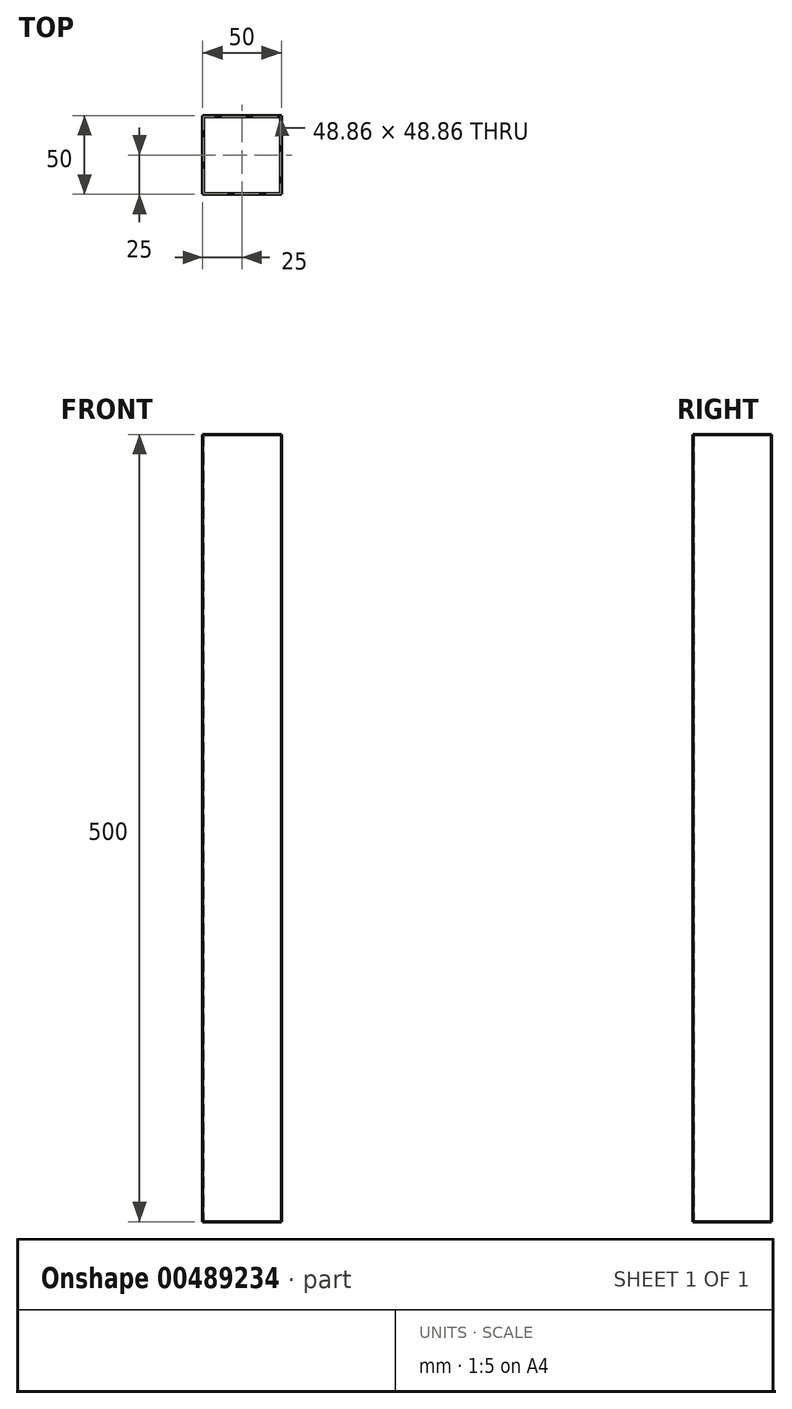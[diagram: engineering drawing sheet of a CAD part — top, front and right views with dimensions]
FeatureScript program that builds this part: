
annotation { "Feature Type Name" : "Feature", "Feature Type Description" : "" }
export const myFeature = defineFeature(function(context is Context, id is Id, definition is map)
    precondition{}
    {
        {
            var Q0;
            Q0=qCreatedBy(makeId("Top.planeOp"),FACE);
            var sketch = newSketch(context, id + "F0", { "sketchPlane" : qUnion([Q0])});
            skLineSegment(sketch, "E0.bottom", {"start": v(0, 0) * mm, "end": v(50, 0) * mm});
            skLineSegment(sketch, "E0.top", {"start": v(0, -50) * mm, "end": v(50, -50) * mm});
            skLineSegment(sketch, "E0.left", {"start": v(0, 0) * mm, "end": v(0, -50) * mm});
            skLineSegment(sketch, "E0.right", {"start": v(50, 0) * mm, "end": v(50, -50) * mm});
            skLineSegment(sketch, "E1.0", {"start": v(0.57, -49.43) * mm, "end": v(49.43, -49.43) * mm});
            skLineSegment(sketch, "E1.1", {"start": v(0.57, -0.57) * mm, "end": v(0.57, -49.43) * mm});
            skLineSegment(sketch, "E1.2", {"start": v(0.57, -0.57) * mm, "end": v(49.43, -0.57) * mm});
            skLineSegment(sketch, "E1.3", {"start": v(49.43, -0.57) * mm, "end": v(49.43, -49.43) * mm});
            skLineSegment(sketch, "E2.0", {"start": v(2.57, -47.43) * mm, "end": v(47.43, -47.43) * mm});
            skLineSegment(sketch, "E2.1", {"start": v(2.57, -2.57) * mm, "end": v(2.57, -47.43) * mm});
            skLineSegment(sketch, "E2.2", {"start": v(2.57, -2.57) * mm, "end": v(47.43, -2.57) * mm});
            skLineSegment(sketch, "E2.3", {"start": v(47.43, -2.57) * mm, "end": v(47.43, -47.43) * mm});
            skSolve(sketch);
        }
        {
            var Q0;
            Q0 = qSketchRegion(id + "F0", true);
            extrude(context, id + "F1", {"entities" : qUnion([Q0]), "depth" : 500 * mm});
        }
    });
